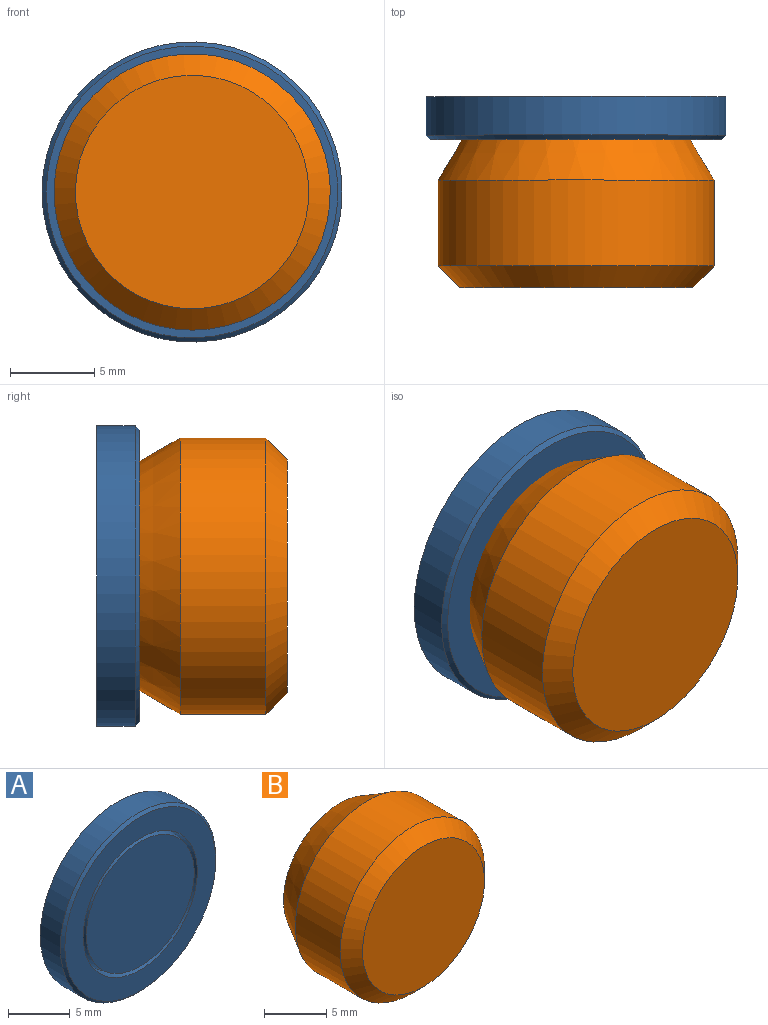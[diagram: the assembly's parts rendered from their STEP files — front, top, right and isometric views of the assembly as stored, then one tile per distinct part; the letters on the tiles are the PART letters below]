
ASSEMBLY  parts=2 mates=1
PART A: 7 faces, bbox 17.8x2.5x17.8 mm
  f0: plane 17.78x17.78mm, normal (0,1,0), area 248.3mm2, adj f6
  f1: plane 12.34x12.34mm, normal (0,-1,0), area 119.6mm2, adj f2
  f2: cone r=6.35mm half-angle=10deg, axis (0,1,0), area 40.6mm2, adj f1,f3
  f3: cone r=6.53mm half-angle=10deg, axis (0,-1,0), area 41.7mm2, adj f2,f4
  f4: plane 17.27x17.27mm, normal (0,-1,0), area 100.4mm2, adj f3,f5
  f5: cone r=8.89mm half-angle=45deg, axis (0,1,0), area 19.8mm2, adj f4,f6
  f6: cylinder r=8.89mm len=17.78mm, axis (0,1,0), area 127.7mm2, adj f0,f5
PART B: 6 faces, bbox 16.4x9.5x16.4 mm
  f0: cone r=4.52mm half-angle=30deg, axis (0,1,0), area 125.2mm2, adj f1,f5
  f1: plane 9.03x9.03mm, normal (0,1,0), area 64.1mm2, adj f0
  f2: plane 13.83x13.83mm, normal (0,-1,0), area 150.1mm2, adj f3
  f3: cone r=8.18mm half-angle=45deg, axis (0,1,0), area 85.2mm2, adj f2,f4
  f4: cylinder r=8.18mm len=16.37mm, axis (0,-1,0), area 261.2mm2, adj f3,f5
  f5: cone r=6.35mm half-angle=30deg, axis (0,-1,0), area 167.4mm2, adj f0,f4
PLACE A t=(0,2.29,0)mm
PLACE B t=(0,-2.67,0)mm
MATE slider B.f0 <-> A.f5  axis (0,-1,0) through (0,-5.21,0)mm
